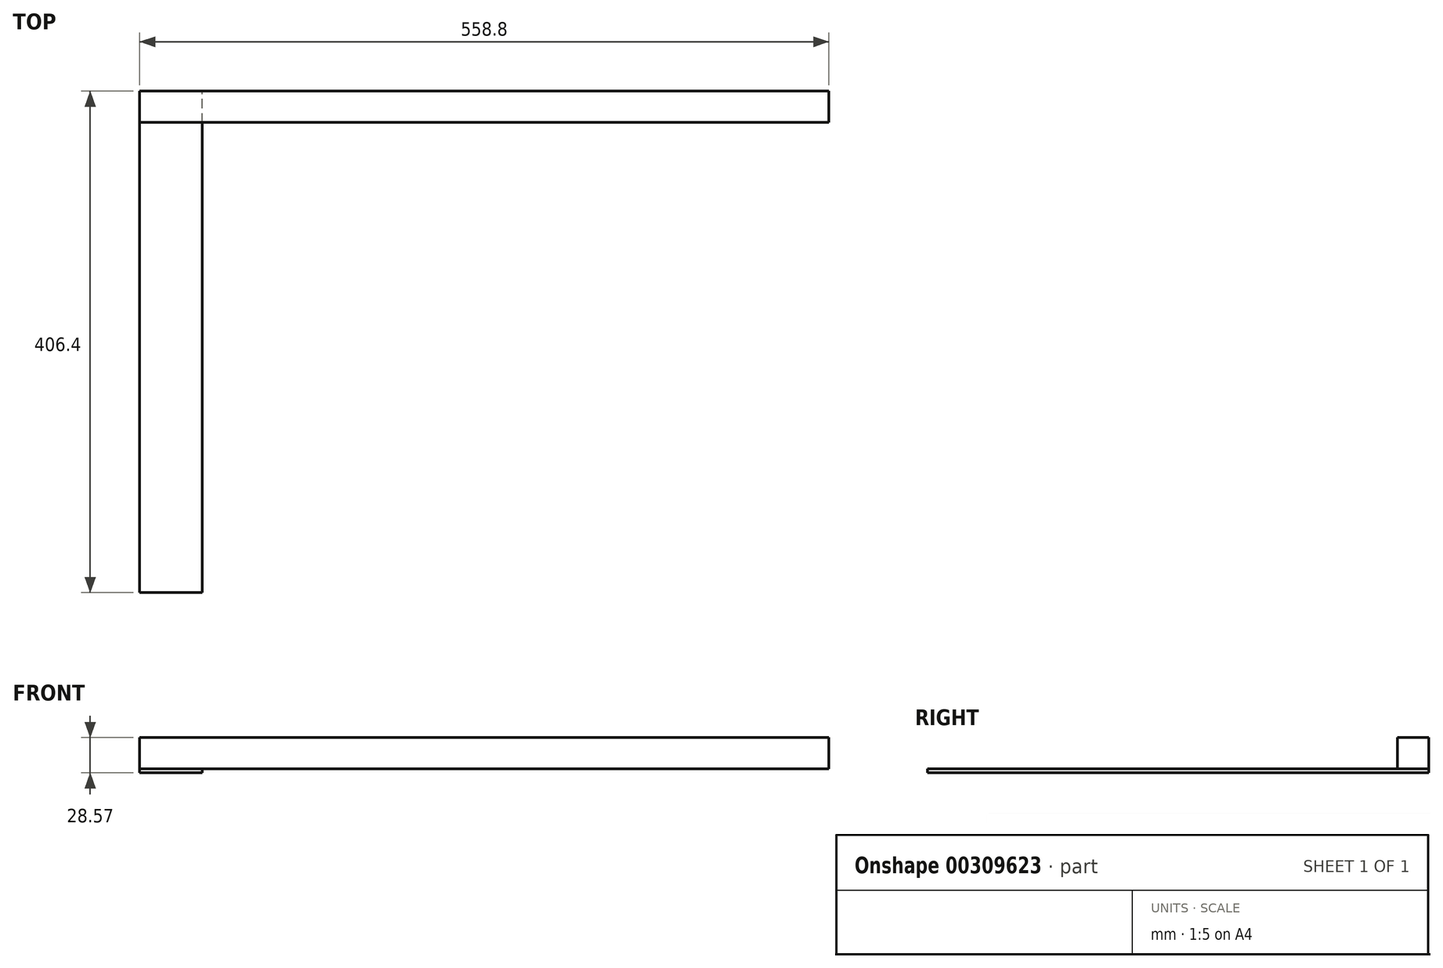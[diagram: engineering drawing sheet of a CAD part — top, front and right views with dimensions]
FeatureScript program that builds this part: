
annotation { "Feature Type Name" : "Feature", "Feature Type Description" : "" }
export const myFeature = defineFeature(function(context is Context, id is Id, definition is map)
    precondition{}
    {
        {
            var Q0;
            Q0=qCreatedBy(makeId("Top.planeOp"),FACE);
            var sketch = newSketch(context, id + "F0", { "sketchPlane" : qUnion([Q0])});
            skLineSegment(sketch, "E0.bottom", {"start": v(0, 0) * mm, "end": v(50.8, 0) * mm});
            skLineSegment(sketch, "E0.top", {"start": v(0, 406.4) * mm, "end": v(50.8, 406.4) * mm});
            skLineSegment(sketch, "E0.left", {"start": v(0, 0) * mm, "end": v(0, 406.4) * mm});
            skLineSegment(sketch, "E0.right", {"start": v(50.8, 0) * mm, "end": v(50.8, 406.4) * mm});
            skSolve(sketch);
        }
        {
            var Q0;
            Q0 = qSketchRegion(id + "F0", true);
            extrude(context, id + "F1", {"entities" : qUnion([Q0]), "depth" : 3.17 * mm});
        }
        {
            var Q0;
            Q0=makeQuery(id+"F1.opExtrude","SWEPT_FACE",FACE,{"disambiguationData":[OSD([sQuery(id+"F0.wireOp",EDGE,"E0.left")])]});
            var sketch = newSketch(context, id + "F2", { "sketchPlane" : qUnion([Q0])});
            skLineSegment(sketch, "E1.bottom", {"start": v(-406.4, 3.18) * mm, "end": v(-381, 3.18) * mm});
            skLineSegment(sketch, "E1.top", {"start": v(-406.4, 28.58) * mm, "end": v(-381, 28.58) * mm});
            skLineSegment(sketch, "E1.left", {"start": v(-406.4, 3.18) * mm, "end": v(-406.4, 28.58) * mm});
            skLineSegment(sketch, "E1.right", {"start": v(-381, 3.18) * mm, "end": v(-381, 28.58) * mm});
            skSolve(sketch);
        }
        {
            var Q0;
            Q0=makeQuery(id+"F2.imprint","IMPRINT",FACE,{"disambiguationData":[TD([[makeQuery(id+"F2.imprint","IMPRINT",EDGE,{"derivedFrom":sQuery(id+"F2.wireOp",EDGE,"E1.bottom")}),-1.0]])]});
            extrude(context, id + "F3", {"entities" : qUnion([Q0]), "operationType" : NewBodyOperationType.ADD, "oppositeDirection" : true, "depth" : 558.8 * mm});
        }
    });
